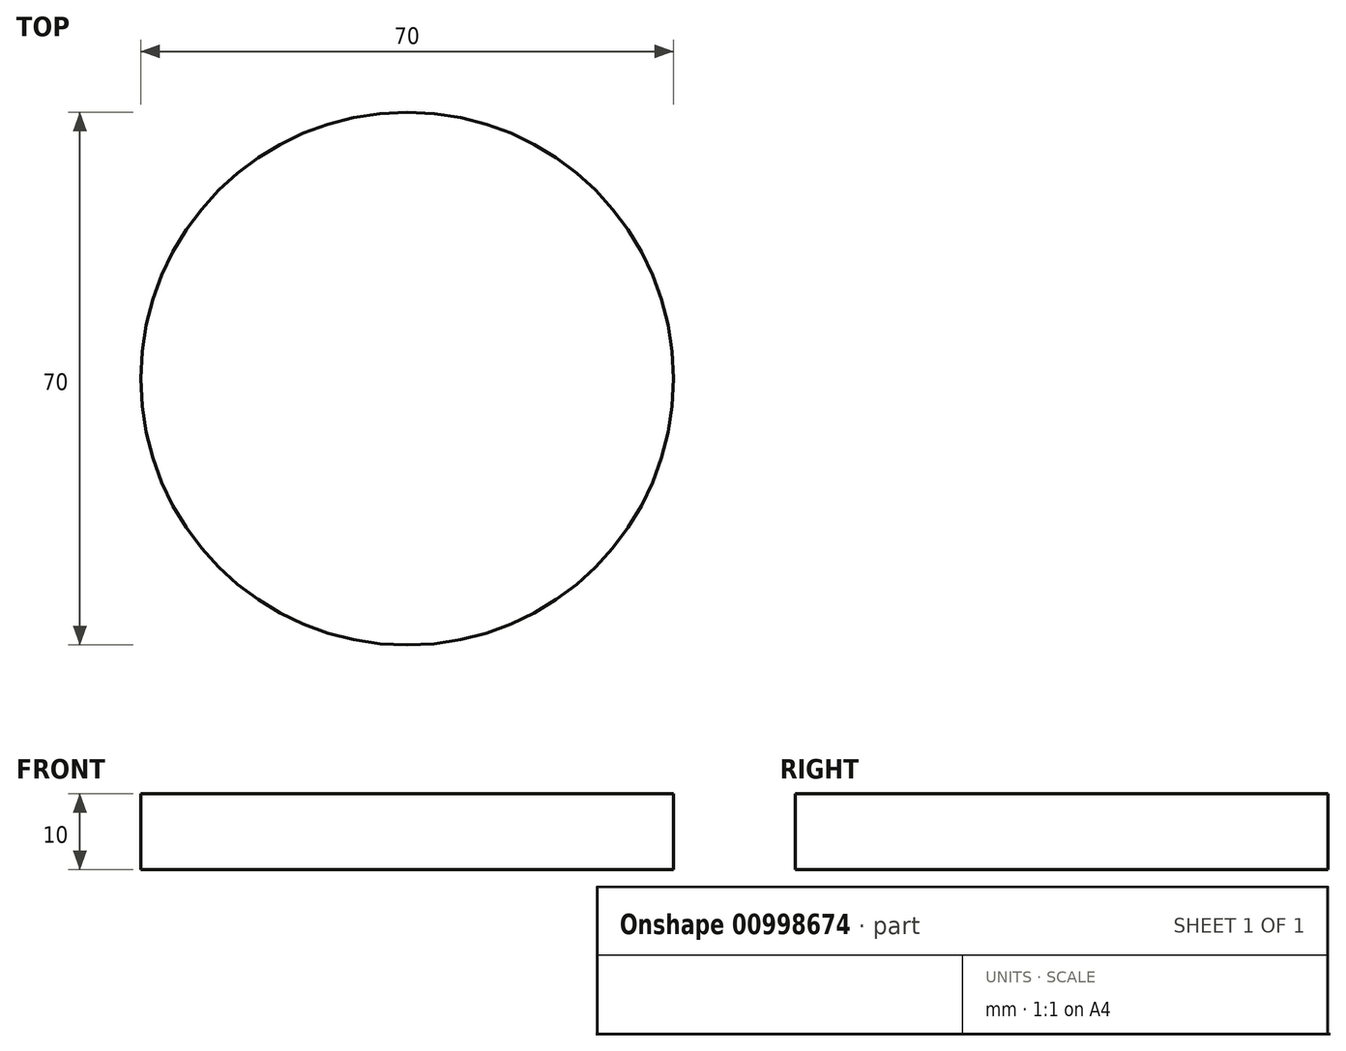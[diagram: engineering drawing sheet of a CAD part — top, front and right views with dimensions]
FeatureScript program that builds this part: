
annotation { "Feature Type Name" : "Feature", "Feature Type Description" : "" }
export const myFeature = defineFeature(function(context is Context, id is Id, definition is map)
    precondition{}
    {
        {
            var Q0;
            Q0=qCreatedBy(makeId("Top.planeOp"),FACE);
            var sketch = newSketch(context, id + "F0", { "sketchPlane" : qUnion([Q0])});
            skCircle(sketch, "E0", {"center": v(0, 0) * mm, "radius": 35 * mm});
            skSolve(sketch);
        }
        {
            var Q0;
            Q0=qSketchRegion(id+"F0",true);
            extrude(context, id + "F1", {"entities" : qUnion([Q0]), "depth" : 10 * mm, "offsetDistance" : 25 * mm});
        }
    });
